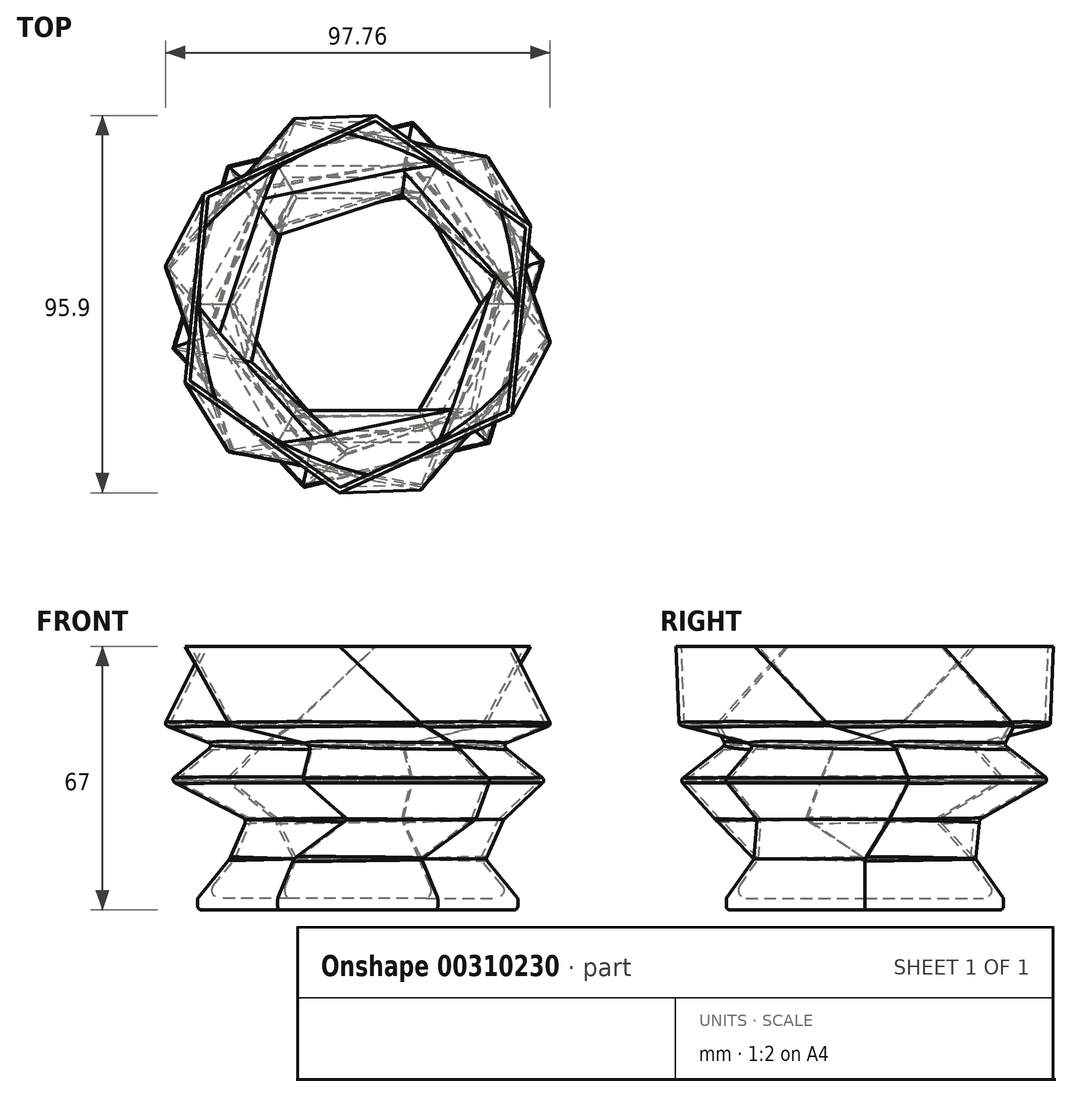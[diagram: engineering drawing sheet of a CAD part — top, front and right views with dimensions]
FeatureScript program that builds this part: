
annotation { "Feature Type Name" : "Feature", "Feature Type Description" : "" }
export const myFeature = defineFeature(function(context is Context, id is Id, definition is map)
    precondition{}
    {
        {
            var Q0;
            Q0=qCreatedBy(makeId("Top.planeOp"),FACE);
            cPlane(context, id + "F0", {"entities" : qUnion([Q0]), "cplaneType" : CPlaneType.OFFSET, "offset" : 10 * mm, "width" : 150 * mm, "height" : 150 * mm});
        }
        {
            var Q0;
            Q0=qCreatedBy(id+"F0.planeOp",FACE);
            cPlane(context, id + "F1", {"entities" : qUnion([Q0]), "cplaneType" : CPlaneType.OFFSET, "offset" : 10 * mm, "width" : 150 * mm, "height" : 150 * mm});
        }
        {
            var Q0;
            Q0=qCreatedBy(id+"F1.planeOp",FACE);
            cPlane(context, id + "F2", {"entities" : qUnion([Q0]), "cplaneType" : CPlaneType.OFFSET, "offset" : 10 * mm, "width" : 150 * mm, "height" : 150 * mm});
        }
        {
            var Q0;
            Q0=qCreatedBy(id+"F2.planeOp",FACE);
            cPlane(context, id + "F3", {"entities" : qUnion([Q0]), "cplaneType" : CPlaneType.OFFSET, "offset" : 9 * mm, "width" : 150 * mm, "height" : 150 * mm});
        }
        {
            var Q0;
            Q0=qCreatedBy(id+"F3.planeOp",FACE);
            cPlane(context, id + "F4", {"entities" : qUnion([Q0]), "cplaneType" : CPlaneType.OFFSET, "offset" : 5 * mm, "width" : 150 * mm, "height" : 150 * mm});
        }
        {
            var Q0;
            Q0=qCreatedBy(id+"F4.planeOp",FACE);
            cPlane(context, id + "F5", {"entities" : qUnion([Q0]), "cplaneType" : CPlaneType.OFFSET, "offset" : 20 * mm, "width" : 150 * mm, "height" : 150 * mm});
        }
        {
            var Q0;
            Q0=qCreatedBy(makeId("Top.planeOp"),FACE);
            var sketch = newSketch(context, id + "F6", { "sketchPlane" : qUnion([Q0])});
            skCircle(sketch, "E0.cCircle", {"center": v(0, 0) * mm, "radius": 40.66 * mm, "construction": true});
            skLineSegment(sketch, "E0.0", {"start": v(-40.66, 0) * mm, "end": v(-20.33, 35.21) * mm});
            skLineSegment(sketch, "E0.1", {"start": v(-20.33, 35.21) * mm, "end": v(20.33, 35.21) * mm});
            skLineSegment(sketch, "E0.2", {"start": v(20.33, 35.21) * mm, "end": v(40.66, 0) * mm});
            skLineSegment(sketch, "E0.3", {"start": v(40.66, 0) * mm, "end": v(20.33, -35.21) * mm});
            skLineSegment(sketch, "E0.4", {"start": v(20.33, -35.21) * mm, "end": v(-20.33, -35.21) * mm});
            skLineSegment(sketch, "E0.5", {"start": v(-20.33, -35.21) * mm, "end": v(-40.66, 0) * mm});
            skSolve(sketch);
        }
        {
            var Q0;
            Q0=qCreatedBy(makeId("Top.planeOp"),FACE);
            var sketch = newSketch(context, id + "F7", { "sketchPlane" : qUnion([Q0])});
            skLineSegment(sketch, "E1.0", {"start": v(-19.64, 34.01) * mm, "end": v(-39.28, 0) * mm});
            skLineSegment(sketch, "E1.1", {"start": v(-19.64, -34.01) * mm, "end": v(19.64, -34.01) * mm});
            skLineSegment(sketch, "E1.2", {"start": v(19.64, -34.01) * mm, "end": v(39.28, 0) * mm});
            skLineSegment(sketch, "E1.3", {"start": v(-39.28, 0) * mm, "end": v(-19.64, -34.01) * mm});
            skLineSegment(sketch, "E1.4", {"start": v(39.28, 0) * mm, "end": v(19.64, 34.01) * mm});
            skLineSegment(sketch, "E1.5", {"start": v(19.64, 34.01) * mm, "end": v(-19.64, 34.01) * mm});
            skSolve(sketch);
        }
        {
            var Q0;
            Q0=qCreatedBy(id+"F0.planeOp",FACE);
            var sketch = newSketch(context, id + "F8", { "sketchPlane" : qUnion([Q0])});
            skCircle(sketch, "E2.cCircle", {"center": v(0, 0) * mm, "radius": 32.53 * mm, "construction": true});
            skLineSegment(sketch, "E2.0", {"start": v(-32.53, 0) * mm, "end": v(-16.27, 28.18) * mm});
            skLineSegment(sketch, "E2.1", {"start": v(-16.27, 28.18) * mm, "end": v(16.27, 28.18) * mm});
            skLineSegment(sketch, "E2.2", {"start": v(16.27, 28.18) * mm, "end": v(32.53, 0) * mm});
            skLineSegment(sketch, "E2.3", {"start": v(32.53, 0) * mm, "end": v(16.27, -28.18) * mm});
            skLineSegment(sketch, "E2.4", {"start": v(16.27, -28.18) * mm, "end": v(-16.27, -28.18) * mm});
            skLineSegment(sketch, "E2.5", {"start": v(-16.27, -28.18) * mm, "end": v(-32.53, 0) * mm});
            skSolve(sketch);
        }
        {
            var Q0;
            Q0=qCreatedBy(id+"F0.planeOp",FACE);
            var sketch = newSketch(context, id + "F9", { "sketchPlane" : qUnion([Q0])});
            skLineSegment(sketch, "E3.0", {"start": v(15.57, -26.98) * mm, "end": v(-15.57, -26.98) * mm});
            skLineSegment(sketch, "E3.1", {"start": v(-31.15, 0) * mm, "end": v(-15.57, 26.98) * mm});
            skLineSegment(sketch, "E3.2", {"start": v(-15.57, 26.98) * mm, "end": v(15.57, 26.98) * mm});
            skLineSegment(sketch, "E3.3", {"start": v(-15.57, -26.98) * mm, "end": v(-31.15, 0) * mm});
            skLineSegment(sketch, "E3.4", {"start": v(15.57, 26.98) * mm, "end": v(31.15, 0) * mm});
            skLineSegment(sketch, "E3.5", {"start": v(31.15, 0) * mm, "end": v(15.57, -26.98) * mm});
            skSolve(sketch);
        }
        {
            var Q0;
            Q0 = qSketchRegion(id + "F6", true);
            var Q1;
            Q1 = qSketchRegion(id + "F8", true);
            loft(context, id + "F10", {"sheetProfilesArray" : [{ "sheetProfileEntities" : qUnion([Q0]) }, { "sheetProfileEntities" : qUnion([Q1]) }]});
        }
        {
            var Q1;
            Q1 = qSketchRegion(id + "F7", true);
            var Q2;
            Q2 = qSketchRegion(id + "F9", true);
            loft(context, id + "F11", {"operationType" : NewBodyOperationType.REMOVE, "sheetProfilesArray" : [{ "sheetProfileEntities" : qUnion([Q1]) }, { "sheetProfileEntities" : qUnion([Q2]) }]});
        }
        {
            var Q0;
            Q0=qCreatedBy(id+"F1.planeOp",FACE);
            var sketch = newSketch(context, id + "F12", { "sketchPlane" : qUnion([Q0])});
            skCircle(sketch, "E4.cCircle", {"center": v(4.39, -4.43) * mm, "radius": 34.33 * mm, "construction": true});
            skLineSegment(sketch, "E4.0", {"start": v(-2.7, -38.02) * mm, "end": v(-28.25, -15.09) * mm});
            skLineSegment(sketch, "E4.1", {"start": v(-28.25, -15.09) * mm, "end": v(-21.16, 18.5) * mm});
            skLineSegment(sketch, "E4.2", {"start": v(-21.16, 18.5) * mm, "end": v(11.47, 29.17) * mm});
            skLineSegment(sketch, "E4.3", {"start": v(11.47, 29.17) * mm, "end": v(37.03, 6.24) * mm});
            skLineSegment(sketch, "E4.4", {"start": v(37.03, 6.24) * mm, "end": v(29.94, -27.36) * mm});
            skLineSegment(sketch, "E4.5", {"start": v(29.94, -27.36) * mm, "end": v(-2.7, -38.02) * mm});
            skSolve(sketch);
        }
        {
            var Q0;
            Q0=qCreatedBy(id+"F1.planeOp",FACE);
            var sketch = newSketch(context, id + "F13", { "sketchPlane" : qUnion([Q0])});
            skLineSegment(sketch, "E5.0", {"start": v(-26.93, -14.66) * mm, "end": v(-2.4, -36.67) * mm});
            skLineSegment(sketch, "E5.1", {"start": v(28.91, -26.43) * mm, "end": v(35.7, 5.8) * mm});
            skLineSegment(sketch, "E5.2", {"start": v(35.7, 5.8) * mm, "end": v(11.19, 27.81) * mm});
            skLineSegment(sketch, "E5.3", {"start": v(-2.4, -36.67) * mm, "end": v(28.91, -26.43) * mm});
            skLineSegment(sketch, "E5.4", {"start": v(11.19, 27.81) * mm, "end": v(-20.13, 17.58) * mm});
            skLineSegment(sketch, "E5.5", {"start": v(-20.13, 17.58) * mm, "end": v(-26.93, -14.66) * mm});
            skSolve(sketch);
        }
        {
            var Q0;
            Q0=qSketchRegion(id+"F8",true);
            var Q1;
            Q1=qSketchRegion(id+"F12",true);
            loft(context, id + "F14", {"operationType" : NewBodyOperationType.ADD, "sheetProfilesArray" : [{ "sheetProfileEntities" : qUnion([Q0]) }, { "sheetProfileEntities" : qUnion([Q1]) }]});
        }
        {
            var Q1;
            Q1=qSketchRegion(id+"F9",true);
            var Q2;
            Q2=qSketchRegion(id+"F13",true);
            loft(context, id + "F15", {"operationType" : NewBodyOperationType.REMOVE, "sheetProfilesArray" : [{ "sheetProfileEntities" : qUnion([Q1]) }, { "sheetProfileEntities" : qUnion([Q2]) }]});
        }
        {
            var Q0;
            Q0=qCreatedBy(id+"F2.planeOp",FACE);
            var sketch = newSketch(context, id + "F16", { "sketchPlane" : qUnion([Q0])});
            skCircle(sketch, "E6.cCircle", {"center": v(0, 0) * mm, "radius": 42.44 * mm, "construction": true});
            skLineSegment(sketch, "E6.0", {"start": v(-14.06, -46.94) * mm, "end": v(-47.68, -11.3) * mm});
            skLineSegment(sketch, "E6.1", {"start": v(-47.68, -11.3) * mm, "end": v(-33.62, 35.65) * mm});
            skLineSegment(sketch, "E6.2", {"start": v(-33.62, 35.65) * mm, "end": v(14.06, 46.94) * mm});
            skLineSegment(sketch, "E6.3", {"start": v(14.06, 46.94) * mm, "end": v(47.68, 11.3) * mm});
            skLineSegment(sketch, "E6.4", {"start": v(47.68, 11.3) * mm, "end": v(33.62, -35.65) * mm});
            skLineSegment(sketch, "E6.5", {"start": v(33.62, -35.65) * mm, "end": v(-14.06, -46.94) * mm});
            skPoint(sketch, "E6.0.midPoint", {"position": v(-30.87, -29.12) * mm});
            skSolve(sketch);
        }
        {
            var Q0;
            Q0=qCreatedBy(id+"F2.planeOp",FACE);
            var sketch = newSketch(context, id + "F17", { "sketchPlane" : qUnion([Q0])});
            skLineSegment(sketch, "E7.0", {"start": v(-46.34, -10.97) * mm, "end": v(-13.67, -45.61) * mm});
            skLineSegment(sketch, "E7.1", {"start": v(32.67, -34.64) * mm, "end": v(46.34, 10.97) * mm});
            skLineSegment(sketch, "E7.2", {"start": v(46.34, 10.97) * mm, "end": v(13.67, 45.61) * mm});
            skLineSegment(sketch, "E7.3", {"start": v(-13.67, -45.61) * mm, "end": v(32.67, -34.64) * mm});
            skLineSegment(sketch, "E7.4", {"start": v(13.67, 45.61) * mm, "end": v(-32.67, 34.64) * mm});
            skLineSegment(sketch, "E7.5", {"start": v(-32.67, 34.64) * mm, "end": v(-46.34, -10.97) * mm});
            skSolve(sketch);
        }
        {
            var Q1;
            Q1=qSketchRegion(id+"F12",true);
            var Q2;
            Q2=qSketchRegion(id+"F16",true);
            loft(context, id + "F18", {"operationType" : NewBodyOperationType.ADD, "sheetProfilesArray" : [{ "sheetProfileEntities" : qUnion([Q1]) }, { "sheetProfileEntities" : qUnion([Q2]) }]});
        }
        {
            var Q1;
            Q1 = qSketchRegion(id + "F13", true);
            var Q2;
            Q2 = qSketchRegion(id + "F17", true);
            loft(context, id + "F19", {"operationType" : NewBodyOperationType.REMOVE, "sheetProfilesArray" : [{ "sheetProfileEntities" : qUnion([Q1]) }, { "sheetProfileEntities" : qUnion([Q2]) }]});
        }
        {
            var Q0;
            Q0=qCreatedBy(id+"F3.planeOp",FACE);
            var sketch = newSketch(context, id + "F20", { "sketchPlane" : qUnion([Q0])});
            skCircle(sketch, "E8.cCircle", {"center": v(0, 0) * mm, "radius": 32.3 * mm, "construction": true});
            skLineSegment(sketch, "E8.0", {"start": v(11.75, 35.4) * mm, "end": v(36.53, 7.52) * mm});
            skLineSegment(sketch, "E8.1", {"start": v(36.53, 7.52) * mm, "end": v(24.78, -27.87) * mm});
            skLineSegment(sketch, "E8.2", {"start": v(24.78, -27.87) * mm, "end": v(-11.75, -35.4) * mm});
            skLineSegment(sketch, "E8.3", {"start": v(-11.75, -35.4) * mm, "end": v(-36.53, -7.52) * mm});
            skLineSegment(sketch, "E8.4", {"start": v(-36.53, -7.52) * mm, "end": v(-24.78, 27.87) * mm});
            skLineSegment(sketch, "E8.5", {"start": v(-24.78, 27.87) * mm, "end": v(11.75, 35.4) * mm});
            skPoint(sketch, "E8.0.midPoint", {"position": v(24.14, 21.46) * mm});
            skSolve(sketch);
        }
        {
            var Q0;
            Q0=qCreatedBy(id+"F3.planeOp",FACE);
            var sketch = newSketch(context, id + "F21", { "sketchPlane" : qUnion([Q0])});
            skLineSegment(sketch, "E9.0", {"start": v(23.86, -26.84) * mm, "end": v(-11.31, -34.08) * mm});
            skLineSegment(sketch, "E9.1", {"start": v(-35.17, -7.24) * mm, "end": v(-23.86, 26.84) * mm});
            skLineSegment(sketch, "E9.2", {"start": v(-23.86, 26.84) * mm, "end": v(11.31, 34.08) * mm});
            skLineSegment(sketch, "E9.3", {"start": v(-11.31, -34.08) * mm, "end": v(-35.17, -7.24) * mm});
            skLineSegment(sketch, "E9.4", {"start": v(11.31, 34.08) * mm, "end": v(35.17, 7.24) * mm});
            skLineSegment(sketch, "E9.5", {"start": v(35.17, 7.24) * mm, "end": v(23.86, -26.84) * mm});
            skSolve(sketch);
        }
        {
            var Q1;
            Q1=qSketchRegion(id+"F16",true);
            var Q2;
            Q2=qSketchRegion(id+"F20",true);
            loft(context, id + "F22", {"operationType" : NewBodyOperationType.ADD, "sheetProfilesArray" : [{ "sheetProfileEntities" : qUnion([Q1]) }, { "sheetProfileEntities" : qUnion([Q2]) }]});
        }
        {
            var Q1;
            Q1=qSketchRegion(id+"F17",true);
            var Q2;
            Q2=qSketchRegion(id+"F21",true);
            loft(context, id + "F23", {"operationType" : NewBodyOperationType.REMOVE, "sheetProfilesArray" : [{ "sheetProfileEntities" : qUnion([Q1]) }, { "sheetProfileEntities" : qUnion([Q2]) }]});
        }
        {
            var Q0;
            Q0=qCreatedBy(id+"F4.planeOp",FACE);
            var sketch = newSketch(context, id + "F24", { "sketchPlane" : qUnion([Q0])});
            skCircle(sketch, "E10.cCircle", {"center": v(0, 0) * mm, "radius": 43.3 * mm, "construction": true});
            skLineSegment(sketch, "E10.0", {"start": v(49.15, -9.17) * mm, "end": v(16.63, -47.15) * mm});
            skLineSegment(sketch, "E10.1", {"start": v(16.63, -47.15) * mm, "end": v(-32.52, -37.98) * mm});
            skLineSegment(sketch, "E10.2", {"start": v(-32.52, -37.98) * mm, "end": v(-49.15, 9.17) * mm});
            skLineSegment(sketch, "E10.3", {"start": v(-49.15, 9.17) * mm, "end": v(-16.63, 47.15) * mm});
            skLineSegment(sketch, "E10.4", {"start": v(-16.63, 47.15) * mm, "end": v(32.52, 37.98) * mm});
            skLineSegment(sketch, "E10.5", {"start": v(32.52, 37.98) * mm, "end": v(49.15, -9.17) * mm});
            skPoint(sketch, "E10.0.midPoint", {"position": v(32.9, -28.16) * mm});
            skSolve(sketch);
        }
        {
            var Q0;
            Q0=qCreatedBy(id+"F4.planeOp",FACE);
            var sketch = newSketch(context, id + "F25", { "sketchPlane" : qUnion([Q0])});
            skLineSegment(sketch, "E11.0", {"start": v(-31.62, -36.93) * mm, "end": v(-47.79, 8.92) * mm});
            skLineSegment(sketch, "E11.1", {"start": v(-16.17, 45.84) * mm, "end": v(31.62, 36.93) * mm});
            skLineSegment(sketch, "E11.2", {"start": v(31.62, 36.93) * mm, "end": v(47.79, -8.92) * mm});
            skLineSegment(sketch, "E11.3", {"start": v(-47.79, 8.92) * mm, "end": v(-16.17, 45.84) * mm});
            skLineSegment(sketch, "E11.4", {"start": v(47.79, -8.92) * mm, "end": v(16.17, -45.84) * mm});
            skLineSegment(sketch, "E11.5", {"start": v(16.17, -45.84) * mm, "end": v(-31.62, -36.93) * mm});
            skSolve(sketch);
        }
        {
            var Q0;
            Q0=qSketchRegion(id+"F20",true);
            var Q1;
            Q1=qSketchRegion(id+"F24",true);
            loft(context, id + "F26", {"sheetProfilesArray" : [{ "sheetProfileEntities" : qUnion([Q0]) }, { "sheetProfileEntities" : qUnion([Q1]) }]});
        }
        {
            var Q1;
            Q1=qSketchRegion(id+"F21",true);
            var Q2;
            Q2=qSketchRegion(id+"F25",true);
            loft(context, id + "F27", {"operationType" : NewBodyOperationType.REMOVE, "sheetProfilesArray" : [{ "sheetProfileEntities" : qUnion([Q1]) }, { "sheetProfileEntities" : qUnion([Q2]) }]});
        }
        {
            var Q0;
            Q0=qCreatedBy(id+"F5.planeOp",FACE);
            var sketch = newSketch(context, id + "F28", { "sketchPlane" : qUnion([Q0])});
            skCircle(sketch, "E12.cCircle", {"center": v(0, 0) * mm, "radius": 41.72 * mm, "construction": true});
            skLineSegment(sketch, "E12.0", {"start": v(-43.85, -19.96) * mm, "end": v(-39.2, 28) * mm});
            skLineSegment(sketch, "E12.1", {"start": v(-39.2, 28) * mm, "end": v(4.64, 47.95) * mm});
            skLineSegment(sketch, "E12.2", {"start": v(4.64, 47.95) * mm, "end": v(43.85, 19.96) * mm});
            skLineSegment(sketch, "E12.3", {"start": v(43.85, 19.96) * mm, "end": v(39.2, -28) * mm});
            skLineSegment(sketch, "E12.4", {"start": v(39.2, -28) * mm, "end": v(-4.64, -47.95) * mm});
            skLineSegment(sketch, "E12.5", {"start": v(-4.64, -47.95) * mm, "end": v(-43.85, -19.96) * mm});
            skPoint(sketch, "E12.0.midPoint", {"position": v(-41.53, 4.02) * mm});
            skSolve(sketch);
        }
        {
            var Q0;
            Q0=qCreatedBy(id+"F5.planeOp",FACE);
            var sketch = newSketch(context, id + "F29", { "sketchPlane" : qUnion([Q0])});
            skLineSegment(sketch, "E13.0", {"start": v(42.59, 19.38) * mm, "end": v(38.08, -27.19) * mm});
            skLineSegment(sketch, "E13.1", {"start": v(-4.5, -46.57) * mm, "end": v(-42.59, -19.38) * mm});
            skLineSegment(sketch, "E13.2", {"start": v(-42.59, -19.38) * mm, "end": v(-38.08, 27.19) * mm});
            skLineSegment(sketch, "E13.3", {"start": v(38.08, -27.19) * mm, "end": v(-4.5, -46.57) * mm});
            skLineSegment(sketch, "E13.4", {"start": v(-38.08, 27.19) * mm, "end": v(4.5, 46.57) * mm});
            skLineSegment(sketch, "E13.5", {"start": v(4.5, 46.57) * mm, "end": v(42.59, 19.38) * mm});
            skSolve(sketch);
        }
        {
            var Q1;
            Q1=qSketchRegion(id+"F24",true);
            var Q2;
            Q2=qSketchRegion(id+"F28",true);
            loft(context, id + "F30", {"operationType" : NewBodyOperationType.ADD, "sheetProfilesArray" : [{ "sheetProfileEntities" : qUnion([Q1]) }, { "sheetProfileEntities" : qUnion([Q2]) }]});
        }
        {
            var Q1;
            Q1=qSketchRegion(id+"F25",true);
            var Q2;
            Q2=qSketchRegion(id+"F29",true);
            loft(context, id + "F31", {"operationType" : NewBodyOperationType.REMOVE, "sheetProfilesArray" : [{ "sheetProfileEntities" : qUnion([Q1]) }, { "sheetProfileEntities" : qUnion([Q2]) }]});
        }
        {
            var Q0;
            Q0=qSketchRegion(id+"F6",true);
            extrude(context, id + "F32", {"entities" : qUnion([Q0]), "operationType" : NewBodyOperationType.ADD, "oppositeDirection" : true, "depth" : 3 * mm});
        }
        {
            var Q0;
            Q0=makeQuery(id+"F10.opLoft","SWEPT_BODY",BODY,{"disambiguationData":[OSD([makeQuery(id+"F6.imprint","IMPRINT",FACE,{"disambiguationData":[TD([[makeQuery(id+"F6.imprint","IMPRINT",EDGE,{"derivedFrom":sQuery(id+"F6.wireOp",EDGE,"E0.0")}),-1.0]])]}),makeQuery(id+"F8.imprint","IMPRINT",FACE,{"disambiguationData":[TD([[makeQuery(id+"F8.imprint","IMPRINT",EDGE,{"derivedFrom":sQuery(id+"F8.wireOp",EDGE,"E2.0")}),-1.0]])]})])]});
            var Q1;
            Q1=makeQuery(id+"F26.opLoft","SWEPT_BODY",BODY,{"disambiguationData":[OSD([makeQuery(id+"F20.imprint","IMPRINT",FACE,{"disambiguationData":[TD([[makeQuery(id+"F20.imprint","IMPRINT",EDGE,{"derivedFrom":sQuery(id+"F20.wireOp",EDGE,"E8.0")}),-1.0]])]}),makeQuery(id+"F24.imprint","IMPRINT",FACE,{"disambiguationData":[TD([[makeQuery(id+"F24.imprint","IMPRINT",EDGE,{"derivedFrom":sQuery(id+"F24.wireOp",EDGE,"E10.0")}),-1.0]])]})])]});
            booleanBodies(context, id + "F33", {"operationType" : BooleanOperationType.UNION, "tools" : qUnion([Q0, Q1])});
        }
        {
            var Q0;
            {var subQ0=sQuery(id+"F16.wireOp",EDGE,"E6.4");var subQ1=sQuery(id+"F16.wireOp",EDGE,"E6.3");var subQ2=sQuery(id+"F16.wireOp",EDGE,"E6.2");Q0=makeQuery(id+"F22.boolean.opBoolean","MERGE",EDGE,{"derivedFrom":[makeQuery(id+"F18.opLoft","MID_CAP_EDGE",EDGE,{"disambiguationData":[OSD([subQ2,subQ1,subQ0])],"capPos":1.0}),makeQuery(id+"F22.opLoft","MID_CAP_EDGE",EDGE,{"disambiguationData":[OSD([subQ2,subQ1,subQ0])],"capPos":0.0})]});}
            var Q1;
            {var subQ0=sQuery(id+"F16.wireOp",EDGE,"E6.3");var subQ1=sQuery(id+"F16.wireOp",EDGE,"E6.2");var subQ2=sQuery(id+"F16.wireOp",EDGE,"E6.1");Q1=makeQuery(id+"F22.boolean.opBoolean","MERGE",EDGE,{"derivedFrom":[makeQuery(id+"F18.opLoft","MID_CAP_EDGE",EDGE,{"disambiguationData":[OSD([subQ2,subQ1,subQ0])],"capPos":1.0}),makeQuery(id+"F22.opLoft","MID_CAP_EDGE",EDGE,{"disambiguationData":[OSD([subQ2,subQ1,subQ0])],"capPos":0.0})]});}
            var Q2;
            {var subQ0=sQuery(id+"F6.wireOp",EDGE,"E0.2");Q2=makeQuery(id+"F32.boolean.opBoolean","MERGE",EDGE,{"derivedFrom":[makeQuery(id+"F10.opLoft","MID_CAP_EDGE",EDGE,{"disambiguationData":[OSD([sQuery(id+"F6.wireOp",EDGE,"E0.1"),subQ0,sQuery(id+"F6.wireOp",EDGE,"E0.3")])],"capPos":0.0}),makeQuery(id+"F32.opExtrude","CAP_EDGE",EDGE,{"disambiguationData":[OSD([subQ0])],"isStart":true})]});}
            var Q3;
            {var subQ0=sQuery(id+"F6.wireOp",EDGE,"E0.1");Q3=makeQuery(id+"F32.boolean.opBoolean","MERGE",EDGE,{"derivedFrom":[makeQuery(id+"F10.opLoft","MID_CAP_EDGE",EDGE,{"disambiguationData":[OSD([sQuery(id+"F6.wireOp",EDGE,"E0.0"),subQ0,sQuery(id+"F6.wireOp",EDGE,"E0.2")])],"capPos":0.0}),makeQuery(id+"F32.opExtrude","CAP_EDGE",EDGE,{"disambiguationData":[OSD([subQ0])],"isStart":true})]});}
            var Q4;
            {var subQ0=sQuery(id+"F6.wireOp",EDGE,"E0.0");Q4=makeQuery(id+"F32.boolean.opBoolean","MERGE",EDGE,{"derivedFrom":[makeQuery(id+"F10.opLoft","MID_CAP_EDGE",EDGE,{"disambiguationData":[OSD([subQ0,sQuery(id+"F6.wireOp",EDGE,"E0.1"),sQuery(id+"F6.wireOp",EDGE,"E0.5")])],"capPos":0.0}),makeQuery(id+"F32.opExtrude","CAP_EDGE",EDGE,{"disambiguationData":[OSD([subQ0])],"isStart":true})]});}
            var Q5;
            {var subQ0=sQuery(id+"F6.wireOp",EDGE,"E0.5");Q5=makeQuery(id+"F32.boolean.opBoolean","MERGE",EDGE,{"derivedFrom":[makeQuery(id+"F10.opLoft","MID_CAP_EDGE",EDGE,{"disambiguationData":[OSD([sQuery(id+"F6.wireOp",EDGE,"E0.0"),sQuery(id+"F6.wireOp",EDGE,"E0.4"),subQ0])],"capPos":0.0}),makeQuery(id+"F32.opExtrude","CAP_EDGE",EDGE,{"disambiguationData":[OSD([subQ0])],"isStart":true})]});}
            var Q6;
            {var subQ0=sQuery(id+"F6.wireOp",EDGE,"E0.4");Q6=makeQuery(id+"F32.boolean.opBoolean","MERGE",EDGE,{"derivedFrom":[makeQuery(id+"F10.opLoft","MID_CAP_EDGE",EDGE,{"disambiguationData":[OSD([sQuery(id+"F6.wireOp",EDGE,"E0.3"),subQ0,sQuery(id+"F6.wireOp",EDGE,"E0.5")])],"capPos":0.0}),makeQuery(id+"F32.opExtrude","CAP_EDGE",EDGE,{"disambiguationData":[OSD([subQ0])],"isStart":true})]});}
            var Q7;
            {var subQ0=sQuery(id+"F6.wireOp",EDGE,"E0.3");Q7=makeQuery(id+"F32.boolean.opBoolean","MERGE",EDGE,{"derivedFrom":[makeQuery(id+"F10.opLoft","MID_CAP_EDGE",EDGE,{"disambiguationData":[OSD([sQuery(id+"F6.wireOp",EDGE,"E0.2"),subQ0,sQuery(id+"F6.wireOp",EDGE,"E0.4")])],"capPos":0.0}),makeQuery(id+"F32.opExtrude","CAP_EDGE",EDGE,{"disambiguationData":[OSD([subQ0])],"isStart":true})]});}
            var Q8;
            {var subQ0=sQuery(id+"F16.wireOp",EDGE,"E6.2");var subQ1=sQuery(id+"F16.wireOp",EDGE,"E6.1");var subQ2=sQuery(id+"F16.wireOp",EDGE,"E6.0");Q8=makeQuery(id+"F22.boolean.opBoolean","MERGE",EDGE,{"derivedFrom":[makeQuery(id+"F18.opLoft","MID_CAP_EDGE",EDGE,{"disambiguationData":[OSD([subQ2,subQ1,subQ0])],"capPos":1.0}),makeQuery(id+"F22.opLoft","MID_CAP_EDGE",EDGE,{"disambiguationData":[OSD([subQ2,subQ1,subQ0])],"capPos":0.0})]});}
            var Q9;
            {var subQ0=sQuery(id+"F16.wireOp",EDGE,"E6.5");var subQ1=sQuery(id+"F16.wireOp",EDGE,"E6.1");var subQ2=sQuery(id+"F16.wireOp",EDGE,"E6.0");Q9=makeQuery(id+"F22.boolean.opBoolean","MERGE",EDGE,{"derivedFrom":[makeQuery(id+"F18.opLoft","MID_CAP_EDGE",EDGE,{"disambiguationData":[OSD([subQ2,subQ1,subQ0])],"capPos":1.0}),makeQuery(id+"F22.opLoft","MID_CAP_EDGE",EDGE,{"disambiguationData":[OSD([subQ2,subQ1,subQ0])],"capPos":0.0})]});}
            var Q10;
            {var subQ0=sQuery(id+"F16.wireOp",EDGE,"E6.5");var subQ1=sQuery(id+"F16.wireOp",EDGE,"E6.4");var subQ2=sQuery(id+"F16.wireOp",EDGE,"E6.0");Q10=makeQuery(id+"F22.boolean.opBoolean","MERGE",EDGE,{"derivedFrom":[makeQuery(id+"F18.opLoft","MID_CAP_EDGE",EDGE,{"disambiguationData":[OSD([subQ2,subQ1,subQ0])],"capPos":1.0}),makeQuery(id+"F22.opLoft","MID_CAP_EDGE",EDGE,{"disambiguationData":[OSD([subQ2,subQ1,subQ0])],"capPos":0.0})]});}
            var Q11;
            {var subQ0=sQuery(id+"F24.wireOp",EDGE,"E10.5");var subQ1=sQuery(id+"F24.wireOp",EDGE,"E10.1");var subQ2=sQuery(id+"F24.wireOp",EDGE,"E10.0");Q11=makeQuery(id+"F30.boolean.opBoolean","MERGE",EDGE,{"derivedFrom":[makeQuery(id+"F26.opLoft","MID_CAP_EDGE",EDGE,{"disambiguationData":[OSD([subQ2,subQ1,subQ0])],"capPos":1.0}),makeQuery(id+"F30.opLoft","MID_CAP_EDGE",EDGE,{"disambiguationData":[OSD([subQ2,subQ1,subQ0])],"capPos":0.0})]});}
            var Q12;
            {var subQ0=sQuery(id+"F24.wireOp",EDGE,"E10.2");var subQ1=sQuery(id+"F24.wireOp",EDGE,"E10.1");var subQ2=sQuery(id+"F24.wireOp",EDGE,"E10.0");Q12=makeQuery(id+"F30.boolean.opBoolean","MERGE",EDGE,{"derivedFrom":[makeQuery(id+"F26.opLoft","MID_CAP_EDGE",EDGE,{"disambiguationData":[OSD([subQ2,subQ1,subQ0])],"capPos":1.0}),makeQuery(id+"F30.opLoft","MID_CAP_EDGE",EDGE,{"disambiguationData":[OSD([subQ2,subQ1,subQ0])],"capPos":0.0})]});}
            var Q13;
            {var subQ0=sQuery(id+"F24.wireOp",EDGE,"E10.3");var subQ1=sQuery(id+"F24.wireOp",EDGE,"E10.2");var subQ2=sQuery(id+"F24.wireOp",EDGE,"E10.1");Q13=makeQuery(id+"F30.boolean.opBoolean","MERGE",EDGE,{"derivedFrom":[makeQuery(id+"F26.opLoft","MID_CAP_EDGE",EDGE,{"disambiguationData":[OSD([subQ2,subQ1,subQ0])],"capPos":1.0}),makeQuery(id+"F30.opLoft","MID_CAP_EDGE",EDGE,{"disambiguationData":[OSD([subQ2,subQ1,subQ0])],"capPos":0.0})]});}
            var Q14;
            {var subQ0=sQuery(id+"F24.wireOp",EDGE,"E10.4");var subQ1=sQuery(id+"F24.wireOp",EDGE,"E10.3");var subQ2=sQuery(id+"F24.wireOp",EDGE,"E10.2");Q14=makeQuery(id+"F30.boolean.opBoolean","MERGE",EDGE,{"derivedFrom":[makeQuery(id+"F26.opLoft","MID_CAP_EDGE",EDGE,{"disambiguationData":[OSD([subQ2,subQ1,subQ0])],"capPos":1.0}),makeQuery(id+"F30.opLoft","MID_CAP_EDGE",EDGE,{"disambiguationData":[OSD([subQ2,subQ1,subQ0])],"capPos":0.0})]});}
            var Q15;
            {var subQ0=sQuery(id+"F24.wireOp",EDGE,"E10.5");var subQ1=sQuery(id+"F24.wireOp",EDGE,"E10.4");var subQ2=sQuery(id+"F24.wireOp",EDGE,"E10.3");Q15=makeQuery(id+"F30.boolean.opBoolean","MERGE",EDGE,{"derivedFrom":[makeQuery(id+"F26.opLoft","MID_CAP_EDGE",EDGE,{"disambiguationData":[OSD([subQ2,subQ1,subQ0])],"capPos":1.0}),makeQuery(id+"F30.opLoft","MID_CAP_EDGE",EDGE,{"disambiguationData":[OSD([subQ2,subQ1,subQ0])],"capPos":0.0})]});}
            var Q16;
            {var subQ0=sQuery(id+"F24.wireOp",EDGE,"E10.5");var subQ1=sQuery(id+"F24.wireOp",EDGE,"E10.4");var subQ2=sQuery(id+"F24.wireOp",EDGE,"E10.0");Q16=makeQuery(id+"F30.boolean.opBoolean","MERGE",EDGE,{"derivedFrom":[makeQuery(id+"F26.opLoft","MID_CAP_EDGE",EDGE,{"disambiguationData":[OSD([subQ2,subQ1,subQ0])],"capPos":1.0}),makeQuery(id+"F30.opLoft","MID_CAP_EDGE",EDGE,{"disambiguationData":[OSD([subQ2,subQ1,subQ0])],"capPos":0.0})]});}
            var Q17;
            {var subQ0=sQuery(id+"F16.wireOp",EDGE,"E6.5");var subQ1=sQuery(id+"F16.wireOp",EDGE,"E6.4");var subQ2=sQuery(id+"F16.wireOp",EDGE,"E6.3");Q17=makeQuery(id+"F22.boolean.opBoolean","MERGE",EDGE,{"derivedFrom":[makeQuery(id+"F18.opLoft","MID_CAP_EDGE",EDGE,{"disambiguationData":[OSD([subQ2,subQ1,subQ0])],"capPos":1.0}),makeQuery(id+"F22.opLoft","MID_CAP_EDGE",EDGE,{"disambiguationData":[OSD([subQ2,subQ1,subQ0])],"capPos":0.0})]});}
            var Q18;
            {var subQ0=sQuery(id+"F12.wireOp",EDGE,"E4.3");var subQ1=sQuery(id+"F12.wireOp",EDGE,"E4.2");var subQ2=sQuery(id+"F12.wireOp",EDGE,"E4.1");Q18=makeQuery(id+"F18.boolean.opBoolean","MERGE",EDGE,{"derivedFrom":[makeQuery(id+"F14.opLoft","MID_CAP_EDGE",EDGE,{"disambiguationData":[OSD([subQ2,subQ1,subQ0])],"capPos":1.0}),makeQuery(id+"F18.opLoft","MID_CAP_EDGE",EDGE,{"disambiguationData":[OSD([subQ2,subQ1,subQ0])],"capPos":0.0})]});}
            var Q19;
            {var subQ0=sQuery(id+"F12.wireOp",EDGE,"E4.4");var subQ1=sQuery(id+"F12.wireOp",EDGE,"E4.3");var subQ2=sQuery(id+"F12.wireOp",EDGE,"E4.2");Q19=makeQuery(id+"F18.boolean.opBoolean","MERGE",EDGE,{"derivedFrom":[makeQuery(id+"F14.opLoft","MID_CAP_EDGE",EDGE,{"disambiguationData":[OSD([subQ2,subQ1,subQ0])],"capPos":1.0}),makeQuery(id+"F18.opLoft","MID_CAP_EDGE",EDGE,{"disambiguationData":[OSD([subQ2,subQ1,subQ0])],"capPos":0.0})]});}
            var Q20;
            {var subQ0=sQuery(id+"F8.wireOp",EDGE,"E2.2");var subQ1=sQuery(id+"F8.wireOp",EDGE,"E2.1");var subQ2=sQuery(id+"F8.wireOp",EDGE,"E2.0");Q20=makeQuery(id+"F14.boolean.opBoolean","MERGE",EDGE,{"derivedFrom":[makeQuery(id+"F10.opLoft","MID_CAP_EDGE",EDGE,{"disambiguationData":[OSD([subQ2,subQ1,subQ0])],"capPos":1.0}),makeQuery(id+"F14.opLoft","MID_CAP_EDGE",EDGE,{"disambiguationData":[OSD([subQ2,subQ1,subQ0])],"capPos":0.0})]});}
            var Q21;
            {var subQ0=sQuery(id+"F8.wireOp",EDGE,"E2.3");var subQ1=sQuery(id+"F8.wireOp",EDGE,"E2.2");var subQ2=sQuery(id+"F8.wireOp",EDGE,"E2.1");Q21=makeQuery(id+"F14.boolean.opBoolean","MERGE",EDGE,{"derivedFrom":[makeQuery(id+"F10.opLoft","MID_CAP_EDGE",EDGE,{"disambiguationData":[OSD([subQ2,subQ1,subQ0])],"capPos":1.0}),makeQuery(id+"F14.opLoft","MID_CAP_EDGE",EDGE,{"disambiguationData":[OSD([subQ2,subQ1,subQ0])],"capPos":0.0})]});}
            var Q22;
            {var subQ0=sQuery(id+"F8.wireOp",EDGE,"E2.5");var subQ1=sQuery(id+"F8.wireOp",EDGE,"E2.1");var subQ2=sQuery(id+"F8.wireOp",EDGE,"E2.0");Q22=makeQuery(id+"F14.boolean.opBoolean","MERGE",EDGE,{"derivedFrom":[makeQuery(id+"F10.opLoft","MID_CAP_EDGE",EDGE,{"disambiguationData":[OSD([subQ2,subQ1,subQ0])],"capPos":1.0}),makeQuery(id+"F14.opLoft","MID_CAP_EDGE",EDGE,{"disambiguationData":[OSD([subQ2,subQ1,subQ0])],"capPos":0.0})]});}
            var Q23;
            {var subQ0=sQuery(id+"F12.wireOp",EDGE,"E4.2");var subQ1=sQuery(id+"F12.wireOp",EDGE,"E4.1");var subQ2=sQuery(id+"F12.wireOp",EDGE,"E4.0");Q23=makeQuery(id+"F18.boolean.opBoolean","MERGE",EDGE,{"derivedFrom":[makeQuery(id+"F14.opLoft","MID_CAP_EDGE",EDGE,{"disambiguationData":[OSD([subQ2,subQ1,subQ0])],"capPos":1.0}),makeQuery(id+"F18.opLoft","MID_CAP_EDGE",EDGE,{"disambiguationData":[OSD([subQ2,subQ1,subQ0])],"capPos":0.0})]});}
            var Q24;
            {var subQ0=sQuery(id+"F8.wireOp",EDGE,"E2.5");var subQ1=sQuery(id+"F8.wireOp",EDGE,"E2.4");var subQ2=sQuery(id+"F8.wireOp",EDGE,"E2.0");Q24=makeQuery(id+"F14.boolean.opBoolean","MERGE",EDGE,{"derivedFrom":[makeQuery(id+"F10.opLoft","MID_CAP_EDGE",EDGE,{"disambiguationData":[OSD([subQ2,subQ1,subQ0])],"capPos":1.0}),makeQuery(id+"F14.opLoft","MID_CAP_EDGE",EDGE,{"disambiguationData":[OSD([subQ2,subQ1,subQ0])],"capPos":0.0})]});}
            var Q25;
            {var subQ0=sQuery(id+"F12.wireOp",EDGE,"E4.5");var subQ1=sQuery(id+"F12.wireOp",EDGE,"E4.1");var subQ2=sQuery(id+"F12.wireOp",EDGE,"E4.0");Q25=makeQuery(id+"F18.boolean.opBoolean","MERGE",EDGE,{"derivedFrom":[makeQuery(id+"F14.opLoft","MID_CAP_EDGE",EDGE,{"disambiguationData":[OSD([subQ2,subQ1,subQ0])],"capPos":1.0}),makeQuery(id+"F18.opLoft","MID_CAP_EDGE",EDGE,{"disambiguationData":[OSD([subQ2,subQ1,subQ0])],"capPos":0.0})]});}
            var Q26;
            {var subQ0=sQuery(id+"F8.wireOp",EDGE,"E2.5");var subQ1=sQuery(id+"F8.wireOp",EDGE,"E2.4");var subQ2=sQuery(id+"F8.wireOp",EDGE,"E2.3");Q26=makeQuery(id+"F14.boolean.opBoolean","MERGE",EDGE,{"derivedFrom":[makeQuery(id+"F10.opLoft","MID_CAP_EDGE",EDGE,{"disambiguationData":[OSD([subQ2,subQ1,subQ0])],"capPos":1.0}),makeQuery(id+"F14.opLoft","MID_CAP_EDGE",EDGE,{"disambiguationData":[OSD([subQ2,subQ1,subQ0])],"capPos":0.0})]});}
            var Q27;
            {var subQ0=sQuery(id+"F12.wireOp",EDGE,"E4.5");var subQ1=sQuery(id+"F12.wireOp",EDGE,"E4.4");var subQ2=sQuery(id+"F12.wireOp",EDGE,"E4.0");Q27=makeQuery(id+"F18.boolean.opBoolean","MERGE",EDGE,{"derivedFrom":[makeQuery(id+"F14.opLoft","MID_CAP_EDGE",EDGE,{"disambiguationData":[OSD([subQ2,subQ1,subQ0])],"capPos":1.0}),makeQuery(id+"F18.opLoft","MID_CAP_EDGE",EDGE,{"disambiguationData":[OSD([subQ2,subQ1,subQ0])],"capPos":0.0})]});}
            var Q28;
            {var subQ0=sQuery(id+"F20.wireOp",EDGE,"E8.3");var subQ1=sQuery(id+"F20.wireOp",EDGE,"E8.2");var subQ2=sQuery(id+"F20.wireOp",EDGE,"E8.1");Q28=makeQuery(id+"F33.opBoolean","MERGE",EDGE,{"derivedFrom":[makeQuery(id+"F22.opLoft","MID_CAP_EDGE",EDGE,{"disambiguationData":[OSD([subQ2,subQ1,subQ0])],"capPos":1.0}),makeQuery(id+"F26.opLoft","MID_CAP_EDGE",EDGE,{"disambiguationData":[OSD([subQ2,subQ1,subQ0])],"capPos":0.0})]});}
            var Q29;
            {var subQ0=sQuery(id+"F20.wireOp",EDGE,"E8.4");var subQ1=sQuery(id+"F20.wireOp",EDGE,"E8.3");var subQ2=sQuery(id+"F20.wireOp",EDGE,"E8.2");Q29=makeQuery(id+"F33.opBoolean","MERGE",EDGE,{"derivedFrom":[makeQuery(id+"F22.opLoft","MID_CAP_EDGE",EDGE,{"disambiguationData":[OSD([subQ2,subQ1,subQ0])],"capPos":1.0}),makeQuery(id+"F26.opLoft","MID_CAP_EDGE",EDGE,{"disambiguationData":[OSD([subQ2,subQ1,subQ0])],"capPos":0.0})]});}
            var Q30;
            {var subQ0=sQuery(id+"F20.wireOp",EDGE,"E8.2");var subQ1=sQuery(id+"F20.wireOp",EDGE,"E8.1");var subQ2=sQuery(id+"F20.wireOp",EDGE,"E8.0");Q30=makeQuery(id+"F33.opBoolean","MERGE",EDGE,{"derivedFrom":[makeQuery(id+"F22.opLoft","MID_CAP_EDGE",EDGE,{"disambiguationData":[OSD([subQ2,subQ1,subQ0])],"capPos":1.0}),makeQuery(id+"F26.opLoft","MID_CAP_EDGE",EDGE,{"disambiguationData":[OSD([subQ2,subQ1,subQ0])],"capPos":0.0})]});}
            var Q31;
            {var subQ0=sQuery(id+"F20.wireOp",EDGE,"E8.5");var subQ1=sQuery(id+"F20.wireOp",EDGE,"E8.1");var subQ2=sQuery(id+"F20.wireOp",EDGE,"E8.0");Q31=makeQuery(id+"F33.opBoolean","MERGE",EDGE,{"derivedFrom":[makeQuery(id+"F22.opLoft","MID_CAP_EDGE",EDGE,{"disambiguationData":[OSD([subQ2,subQ1,subQ0])],"capPos":1.0}),makeQuery(id+"F26.opLoft","MID_CAP_EDGE",EDGE,{"disambiguationData":[OSD([subQ2,subQ1,subQ0])],"capPos":0.0})]});}
            var Q32;
            {var subQ0=sQuery(id+"F20.wireOp",EDGE,"E8.5");var subQ1=sQuery(id+"F20.wireOp",EDGE,"E8.4");var subQ2=sQuery(id+"F20.wireOp",EDGE,"E8.0");Q32=makeQuery(id+"F33.opBoolean","MERGE",EDGE,{"derivedFrom":[makeQuery(id+"F22.opLoft","MID_CAP_EDGE",EDGE,{"disambiguationData":[OSD([subQ2,subQ1,subQ0])],"capPos":1.0}),makeQuery(id+"F26.opLoft","MID_CAP_EDGE",EDGE,{"disambiguationData":[OSD([subQ2,subQ1,subQ0])],"capPos":0.0})]});}
            var Q33;
            {var subQ0=sQuery(id+"F20.wireOp",EDGE,"E8.5");var subQ1=sQuery(id+"F20.wireOp",EDGE,"E8.4");var subQ2=sQuery(id+"F20.wireOp",EDGE,"E8.3");Q33=makeQuery(id+"F33.opBoolean","MERGE",EDGE,{"derivedFrom":[makeQuery(id+"F22.opLoft","MID_CAP_EDGE",EDGE,{"disambiguationData":[OSD([subQ2,subQ1,subQ0])],"capPos":1.0}),makeQuery(id+"F26.opLoft","MID_CAP_EDGE",EDGE,{"disambiguationData":[OSD([subQ2,subQ1,subQ0])],"capPos":0.0})]});}
            var Q34;
            Q34=makeQuery(id+"F32.opExtrude","CAP_FACE",FACE,{"disambiguationData":[OSD([sQuery(id+"F6.wireOp",EDGE,"E0.0"),sQuery(id+"F6.wireOp",EDGE,"E0.1"),sQuery(id+"F6.wireOp",EDGE,"E0.2"),sQuery(id+"F6.wireOp",EDGE,"E0.3"),sQuery(id+"F6.wireOp",EDGE,"E0.4"),sQuery(id+"F6.wireOp",EDGE,"E0.5")])],"isStart":false});
            var Q35;
            Q35=makeQuery(id+"F31.boolean.opBoolean","COPY",EDGE,{"derivedFrom":makeQuery(id+"F31.opLoft","MID_CAP_EDGE",EDGE,{"disambiguationData":[OSD([sQuery(id+"F29.wireOp",EDGE,"E13.1"),sQuery(id+"F29.wireOp",EDGE,"E13.2"),sQuery(id+"F29.wireOp",EDGE,"E13.4")])],"capPos":1.0})});
            var Q36;
            Q36=makeQuery(id+"F31.boolean.opBoolean","COPY",EDGE,{"derivedFrom":makeQuery(id+"F31.opLoft","MID_CAP_EDGE",EDGE,{"disambiguationData":[OSD([sQuery(id+"F29.wireOp",EDGE,"E13.2"),sQuery(id+"F29.wireOp",EDGE,"E13.4"),sQuery(id+"F29.wireOp",EDGE,"E13.5")])],"capPos":1.0})});
            var Q37;
            Q37=makeQuery(id+"F31.boolean.opBoolean","COPY",EDGE,{"derivedFrom":makeQuery(id+"F31.opLoft","MID_CAP_EDGE",EDGE,{"disambiguationData":[OSD([sQuery(id+"F29.wireOp",EDGE,"E13.0"),sQuery(id+"F29.wireOp",EDGE,"E13.4"),sQuery(id+"F29.wireOp",EDGE,"E13.5")])],"capPos":1.0})});
            var Q38;
            Q38=makeQuery(id+"F31.boolean.opBoolean","COPY",EDGE,{"derivedFrom":makeQuery(id+"F31.opLoft","MID_CAP_EDGE",EDGE,{"disambiguationData":[OSD([sQuery(id+"F29.wireOp",EDGE,"E13.0"),sQuery(id+"F29.wireOp",EDGE,"E13.3"),sQuery(id+"F29.wireOp",EDGE,"E13.5")])],"capPos":1.0})});
            var Q39;
            Q39=makeQuery(id+"F31.boolean.opBoolean","COPY",EDGE,{"derivedFrom":makeQuery(id+"F31.opLoft","MID_CAP_EDGE",EDGE,{"disambiguationData":[OSD([sQuery(id+"F29.wireOp",EDGE,"E13.0"),sQuery(id+"F29.wireOp",EDGE,"E13.1"),sQuery(id+"F29.wireOp",EDGE,"E13.3")])],"capPos":1.0})});
            var Q40;
            Q40=makeQuery(id+"F31.boolean.opBoolean","COPY",EDGE,{"derivedFrom":makeQuery(id+"F31.opLoft","MID_CAP_EDGE",EDGE,{"disambiguationData":[OSD([sQuery(id+"F29.wireOp",EDGE,"E13.1"),sQuery(id+"F29.wireOp",EDGE,"E13.2"),sQuery(id+"F29.wireOp",EDGE,"E13.3")])],"capPos":1.0})});
            fillet(context, id + "F34", {"entities" : qUnion([Q0, Q1, Q2, Q3, Q4, Q5, Q6, Q7, Q8, Q9, Q10, Q11, Q12, Q13, Q14, Q15, Q16, Q17, Q18, Q19, Q20, Q21, Q22, Q23, Q24, Q25, Q26, Q27, Q28, Q29, Q30, Q31, Q32, Q33, Q34, Q35, Q36, Q37, Q38, Q39, Q40]), "radius" : 1 * mm, "tangentPropagation" : true, "allowEdgeOverflow" : false});
        }
        {
            var Q0;
            Q0=makeQuery(id+"F32.opExtrude","CAP_FACE",FACE,{"disambiguationData":[OSD([sQuery(id+"F6.wireOp",EDGE,"E0.0"),sQuery(id+"F6.wireOp",EDGE,"E0.1"),sQuery(id+"F6.wireOp",EDGE,"E0.2"),sQuery(id+"F6.wireOp",EDGE,"E0.3"),sQuery(id+"F6.wireOp",EDGE,"E0.4"),sQuery(id+"F6.wireOp",EDGE,"E0.5")])],"isStart":true});
            fillet(context, id + "F35", {"entities" : qUnion([Q0]), "radius" : 2 * mm, "tangentPropagation" : true, "allowEdgeOverflow" : false});
        }
    });
